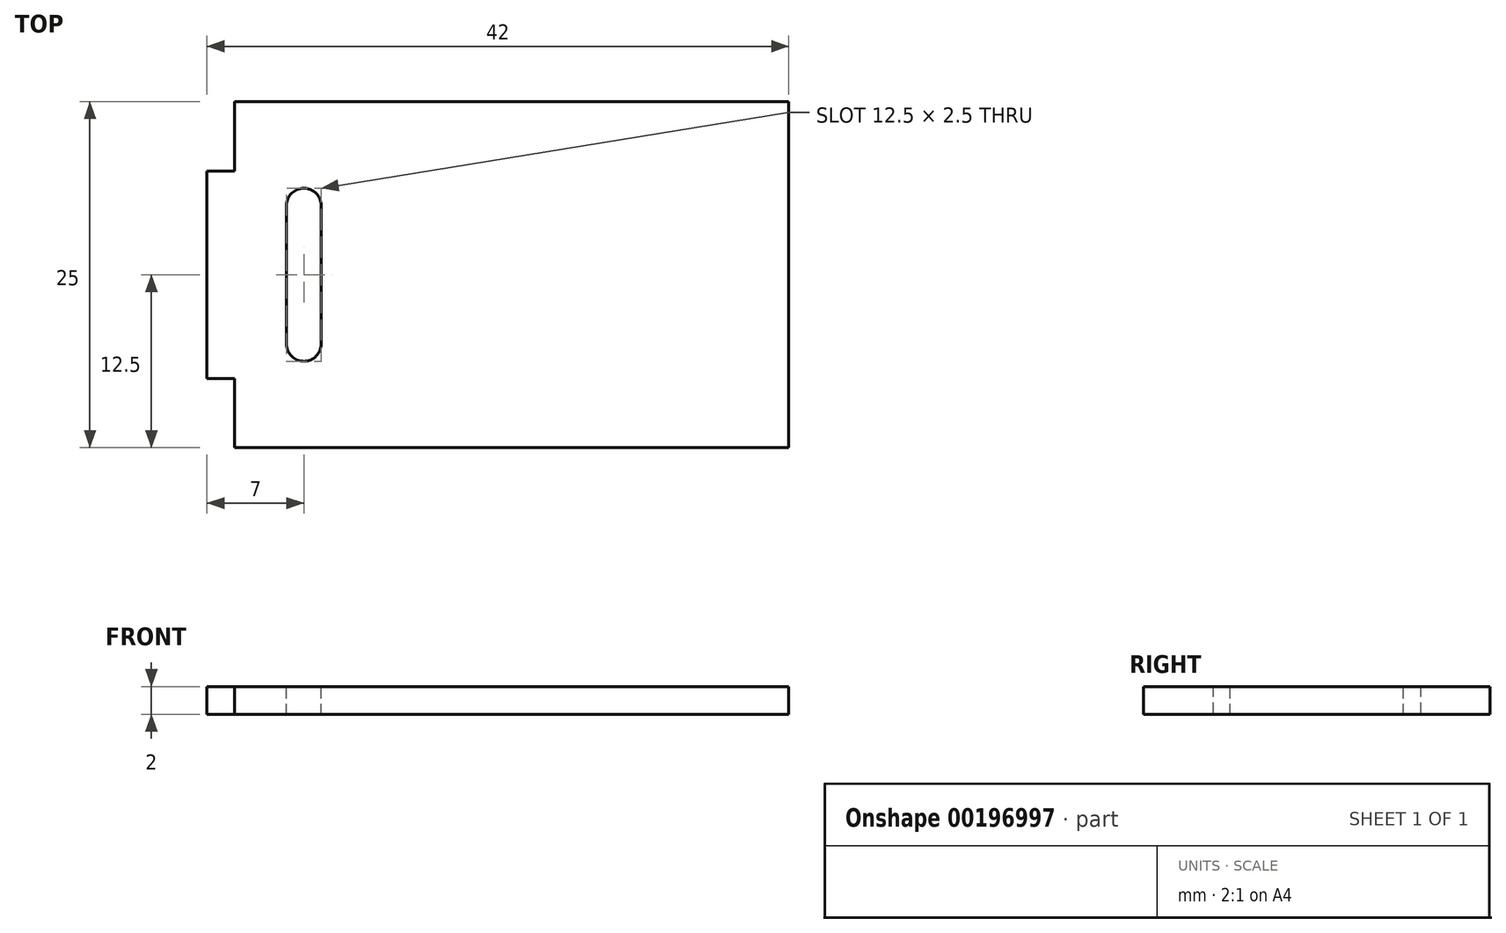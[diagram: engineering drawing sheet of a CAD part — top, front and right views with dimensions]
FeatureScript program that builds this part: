
annotation { "Feature Type Name" : "Feature", "Feature Type Description" : "" }
export const myFeature = defineFeature(function(context is Context, id is Id, definition is map)
    precondition{}
    {
        {
            var Q0;
            Q0=qCreatedBy(makeId("Top.planeOp"),FACE);
            var sketch = newSketch(context, id + "F0", { "sketchPlane" : qUnion([Q0])});
            skLineSegment(sketch, "E0.bottom", {"start": v(20, 12.5) * mm, "end": v(-20, 12.5) * mm});
            skLineSegment(sketch, "E0.top", {"start": v(20, -12.5) * mm, "end": v(-20, -12.5) * mm});
            skLineSegment(sketch, "E0.left", {"start": v(20, 12.5) * mm, "end": v(20, -12.5) * mm});
            skLineSegment(sketch, "E0.right", {"start": v(-20, 12.5) * mm, "end": v(-20, -12.5) * mm});
            skPoint(sketch, "E0.middle", {"position": v(0, 0) * mm});
            skSolve(sketch);
        }
        {
            var Q0;
            Q0 = qSketchRegion(id + "F0", true);
            extrude(context, id + "F1", {"entities" : qUnion([Q0]), "depth" : 2 * mm});
        }
        {
            var Q0;
            Q0=qCreatedBy(makeId("Top.planeOp"),FACE);
            var sketch = newSketch(context, id + "F2", { "sketchPlane" : qUnion([Q0])});
            skLineSegment(sketch, "E1", {"start": v(0, 0) * mm, "end": v(-20, 0) * mm, "construction": true});
            skLineSegment(sketch, "E2.bottom", {"start": v(-20, 7.5) * mm, "end": v(-22, 7.5) * mm});
            skLineSegment(sketch, "E2.top", {"start": v(-20, -7.5) * mm, "end": v(-22, -7.5) * mm});
            skLineSegment(sketch, "E2.left", {"start": v(-20, 7.5) * mm, "end": v(-20, -7.5) * mm});
            skLineSegment(sketch, "E2.right", {"start": v(-22, 7.5) * mm, "end": v(-22, -7.5) * mm});
            skSolve(sketch);
        }
        {
            var Q0;
            Q0 = qSketchRegion(id + "F2", true);
            extrude(context, id + "F3", {"entities" : qUnion([Q0]), "operationType" : NewBodyOperationType.ADD, "depth" : 2 * mm});
        }
        {
            var Q0;
            {var subQ0=sQuery(id+"F2.wireOp",EDGE,"E2.right");var subQ1=sQuery(id+"F2.wireOp",EDGE,"E2.left");var subQ2=sQuery(id+"F2.wireOp",EDGE,"E2.top");var subQ3=sQuery(id+"F2.wireOp",EDGE,"E2.bottom");Q0=makeQuery(id+"FaRhJeDl5bXZvjD_1.1.F3.boolean.opBoolean","MERGE",FACE,{"derivedFrom":[makeQuery(id+"F3.boolean.opBoolean","MERGE",FACE,{"derivedFrom":[makeQuery(id+"F1.opExtrude","CAP_FACE",FACE,{"disambiguationData":[OSD([sQuery(id+"F0.wireOp",EDGE,"E0.bottom"),sQuery(id+"F0.wireOp",EDGE,"E0.top"),sQuery(id+"F0.wireOp",EDGE,"E0.left"),sQuery(id+"F0.wireOp",EDGE,"E0.right")])],"isStart":false}),makeQuery(id+"F3.opExtrude","CAP_FACE",FACE,{"disambiguationData":[OSD([subQ3,subQ2,subQ1,subQ0])],"isStart":false})]}),makeQuery(id+"FaRhJeDl5bXZvjD_1.1.F3.opExtrude","CAP_FACE",FACE,{"disambiguationData":[OSD([subQ3,subQ2,subQ1,subQ0])],"isStart":false})]});}
            var sketch = newSketch(context, id + "F4", { "sketchPlane" : qUnion([Q0])});
            skLineSegment(sketch, "E3", {"start": v(0, 0) * mm, "end": v(-15, 0) * mm, "construction": true});
            skLineSegment(sketch, "E4", {"start": v(-15, 5) * mm, "end": v(-15, -5) * mm, "construction": true});
            skArc(sketch, "E5.0.startCap", {"start": v(-16.25, 5) * mm, "mid": v(-15, 6.25) * mm, "end": v(-13.75, 5) * mm});
            skArc(sketch, "E5.0.endCap", {"start": v(-13.75, -5) * mm, "mid": v(-15, -6.25) * mm, "end": v(-16.25, -5) * mm});
            skLineSegment(sketch, "E5.0.left", {"start": v(-13.75, 5) * mm, "end": v(-13.75, -5) * mm});
            skLineSegment(sketch, "E5.0.right", {"start": v(-16.25, 5) * mm, "end": v(-16.25, -5) * mm});
            skSolve(sketch);
        }
        {
            var Q0;
            Q0 = qSketchRegion(id + "F4", true);
            extrude(context, id + "F5", {"entities" : qUnion([Q0]), "operationType" : NewBodyOperationType.REMOVE, "endBound" : BoundingType.THROUGH_ALL, "oppositeDirection" : true, "depth" : 25 * mm});
        }
    });
